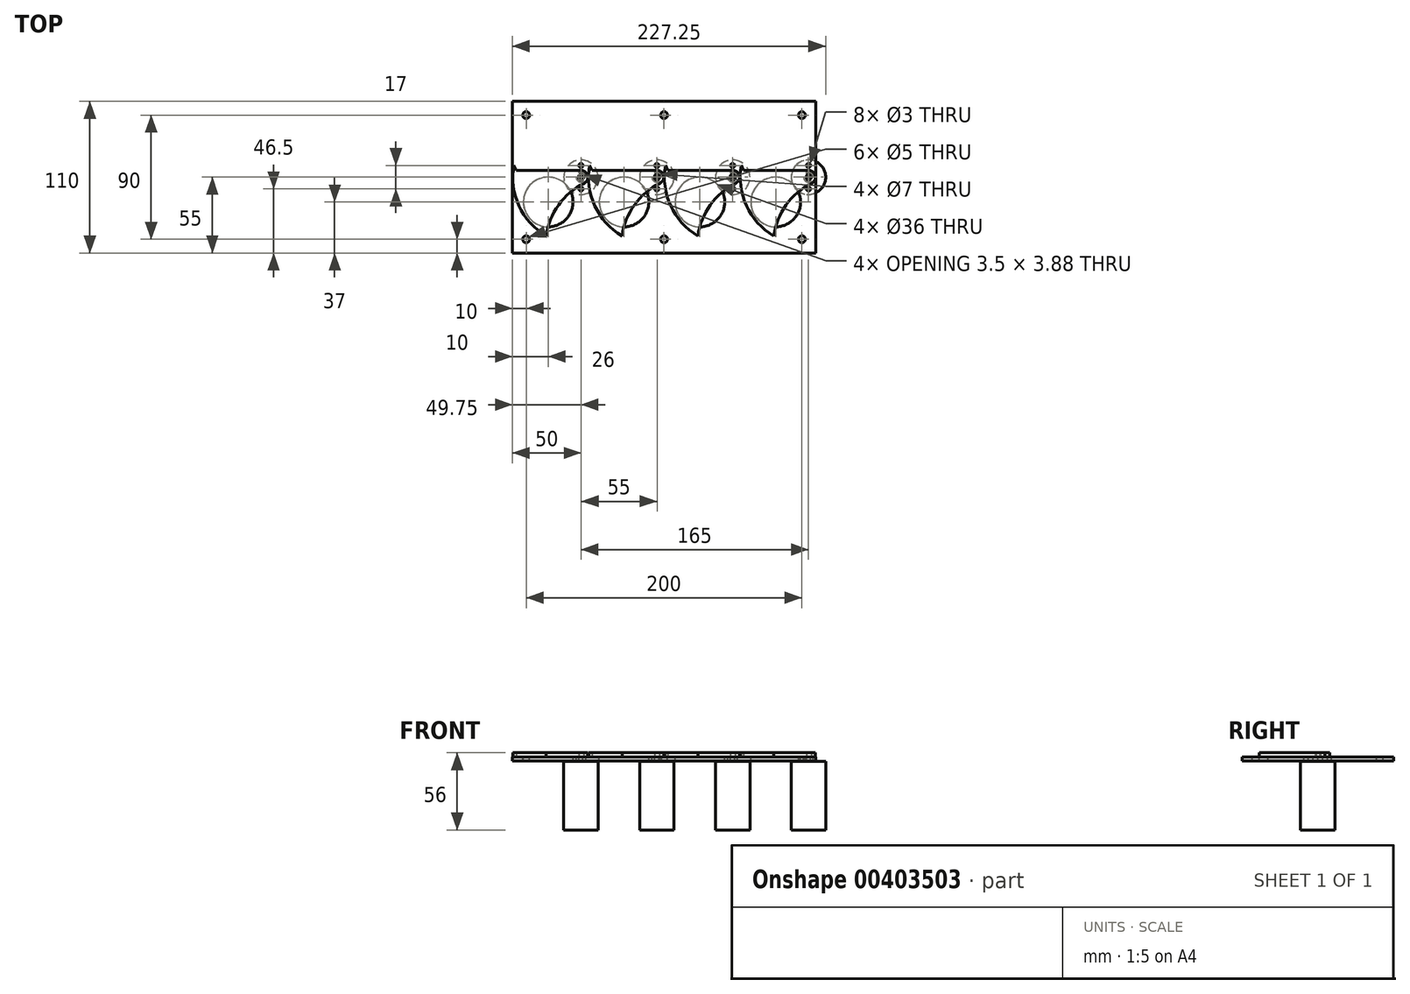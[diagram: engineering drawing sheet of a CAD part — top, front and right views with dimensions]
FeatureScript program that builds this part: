
annotation { "Feature Type Name" : "Feature", "Feature Type Description" : "" }
export const myFeature = defineFeature(function(context is Context, id is Id, definition is map)
    precondition{}
    {
        {
            var Q0;
            Q0=qCreatedBy(makeId("Top.planeOp"),FACE);
            var sketch = newSketch(context, id + "F0", { "sketchPlane" : qUnion([Q0])});
            skPoint(sketch, "E0.middle", {"position": v(0, 0) * mm});
            skLineSegment(sketch, "E1", {"start": v(-48.75, 8.6) * mm, "end": v(-47, 5) * mm});
            skLineSegment(sketch, "E2", {"start": v(-47, 5) * mm, "end": v(0, 5) * mm});
            skArc(sketch, "E3", {"start": v(0, 5) * mm, "mid": v(4.87, 1.14) * mm, "end": v(2.22, -4.48) * mm});
            skArc(sketch, "E4", {"start": v(-48.75, 8.6) * mm, "mid": v(-44.96, -20.7) * mm, "end": v(-25.16, -42.63) * mm});
            skLineSegment(sketch, "E5", {"start": v(-1.5, 1.32) * mm, "end": v(-1.5, -1.32) * mm});
            skArc(sketch, "E6", {"start": v(-1.5, -1.32) * mm, "mid": v(2, 0) * mm, "end": v(-1.5, 1.32) * mm});
            skArc(sketch, "E7", {"start": v(2.22, -4.48) * mm, "mid": v(-16.23, -20.14) * mm, "end": v(-25.16, -42.63) * mm});
            skArc(sketch, "E8.1.0.0", {"start": v(57.22, -4.48) * mm, "mid": v(38.77, -20.14) * mm, "end": v(29.84, -42.63) * mm});
            skArc(sketch, "E8.1.0.1", {"start": v(6.25, 8.6) * mm, "mid": v(10.04, -20.7) * mm, "end": v(29.84, -42.63) * mm});
            skLineSegment(sketch, "E8.1.0.2", {"start": v(8, 5) * mm, "end": v(55, 5) * mm});
            skPoint(sketch, "E8.1.0.3", {"position": v(55, 0) * mm});
            skArc(sketch, "E8.1.0.4", {"start": v(55, 5) * mm, "mid": v(59.87, 1.14) * mm, "end": v(57.22, -4.48) * mm});
            skLineSegment(sketch, "E8.1.0.5", {"start": v(6.25, 8.6) * mm, "end": v(8, 5) * mm});
            skLineSegment(sketch, "E8.1.0.6", {"start": v(53.5, 1.32) * mm, "end": v(53.5, -1.32) * mm});
            skArc(sketch, "E8.1.0.7", {"start": v(53.5, -1.32) * mm, "mid": v(57, 0) * mm, "end": v(53.5, 1.32) * mm});
            skArc(sketch, "E8.2.0.0", {"start": v(112.22, -4.48) * mm, "mid": v(93.77, -20.14) * mm, "end": v(84.84, -42.63) * mm});
            skArc(sketch, "E8.2.0.1", {"start": v(61.25, 8.6) * mm, "mid": v(65.04, -20.7) * mm, "end": v(84.84, -42.63) * mm});
            skLineSegment(sketch, "E8.2.0.2", {"start": v(63, 5) * mm, "end": v(110, 5) * mm});
            skPoint(sketch, "E8.2.0.3", {"position": v(110, 0) * mm});
            skArc(sketch, "E8.2.0.4", {"start": v(110, 5) * mm, "mid": v(114.87, 1.14) * mm, "end": v(112.22, -4.48) * mm});
            skLineSegment(sketch, "E8.2.0.5", {"start": v(61.25, 8.6) * mm, "end": v(63, 5) * mm});
            skLineSegment(sketch, "E8.2.0.6", {"start": v(108.5, 1.32) * mm, "end": v(108.5, -1.32) * mm});
            skArc(sketch, "E8.2.0.7", {"start": v(108.5, -1.32) * mm, "mid": v(112, 0) * mm, "end": v(108.5, 1.32) * mm});
            skArc(sketch, "E8.3.0.0", {"start": v(167.22, -4.48) * mm, "mid": v(148.77, -20.14) * mm, "end": v(139.84, -42.63) * mm});
            skArc(sketch, "E8.3.0.1", {"start": v(116.25, 8.6) * mm, "mid": v(120.04, -20.7) * mm, "end": v(139.84, -42.63) * mm});
            skLineSegment(sketch, "E8.3.0.2", {"start": v(118, 5) * mm, "end": v(165, 5) * mm});
            skPoint(sketch, "E8.3.0.3", {"position": v(165, 0) * mm});
            skArc(sketch, "E8.3.0.4", {"start": v(165, 5) * mm, "mid": v(169.87, 1.14) * mm, "end": v(167.22, -4.48) * mm});
            skLineSegment(sketch, "E8.3.0.5", {"start": v(116.25, 8.6) * mm, "end": v(118, 5) * mm});
            skLineSegment(sketch, "E8.3.0.6", {"start": v(163.5, 1.32) * mm, "end": v(163.5, -1.32) * mm});
            skArc(sketch, "E8.3.0.7", {"start": v(163.5, -1.32) * mm, "mid": v(167, 0) * mm, "end": v(163.5, 1.32) * mm});
            skLineSegment(sketch, "E8.direction1", {"start": v(-25.16, -42.63) * mm, "end": v(29.84, -42.63) * mm, "construction": true});
            skSolve(sketch);
        }
        {
            var Q0;
            Q0=qCreatedBy(makeId("Top.planeOp"),FACE);
            var sketch = newSketch(context, id + "F1", { "sketchPlane" : qUnion([Q0])});
            skCircle(sketch, "E9", {"center": v(0, 0) * mm, "radius": 3.5 * mm});
            skLineSegment(sketch, "E10.bottom", {"start": v(-49.75, 55) * mm, "end": v(170.25, 55) * mm});
            skLineSegment(sketch, "E10.top", {"start": v(-49.75, -55) * mm, "end": v(170.25, -55) * mm});
            skLineSegment(sketch, "E10.left", {"start": v(-49.75, 55) * mm, "end": v(-49.75, -55) * mm});
            skLineSegment(sketch, "E10.right", {"start": v(170.25, 55) * mm, "end": v(170.25, -55) * mm});
            skCircle(sketch, "E11", {"center": v(0, 8.5) * mm, "radius": 1.5 * mm});
            skCircle(sketch, "E12", {"center": v(0, -8.5) * mm, "radius": 1.5 * mm});
            skCircle(sketch, "E13", {"center": v(-39.75, -45) * mm, "radius": 2.5 * mm});
            skCircle(sketch, "E14", {"center": v(60.25, -45) * mm, "radius": 2.5 * mm});
            skCircle(sketch, "E15", {"center": v(160.25, -45) * mm, "radius": 2.5 * mm});
            skCircle(sketch, "E16", {"center": v(-39.75, 45) * mm, "radius": 2.5 * mm});
            skCircle(sketch, "E17", {"center": v(60.25, 45) * mm, "radius": 2.5 * mm});
            skCircle(sketch, "E18", {"center": v(160.25, 45) * mm, "radius": 2.5 * mm});
            skCircle(sketch, "E19", {"center": v(-23.75, -18) * mm, "radius": 18 * mm});
            skCircle(sketch, "E20.1.0.0", {"center": v(55, 0) * mm, "radius": 3.5 * mm});
            skCircle(sketch, "E20.1.0.1", {"center": v(31.25, -18) * mm, "radius": 18 * mm});
            skCircle(sketch, "E20.1.0.2", {"center": v(55, -8.5) * mm, "radius": 1.5 * mm});
            skCircle(sketch, "E20.1.0.3", {"center": v(55, 8.5) * mm, "radius": 1.5 * mm});
            skCircle(sketch, "E20.2.0.0", {"center": v(110, 0) * mm, "radius": 3.5 * mm});
            skCircle(sketch, "E20.2.0.1", {"center": v(86.25, -18) * mm, "radius": 18 * mm});
            skCircle(sketch, "E20.2.0.2", {"center": v(110, -8.5) * mm, "radius": 1.5 * mm});
            skCircle(sketch, "E20.2.0.3", {"center": v(110, 8.5) * mm, "radius": 1.5 * mm});
            skCircle(sketch, "E20.3.0.0", {"center": v(165, 0) * mm, "radius": 3.5 * mm});
            skCircle(sketch, "E20.3.0.1", {"center": v(141.25, -18) * mm, "radius": 18 * mm});
            skCircle(sketch, "E20.3.0.2", {"center": v(165, -8.5) * mm, "radius": 1.5 * mm});
            skCircle(sketch, "E20.3.0.3", {"center": v(165, 8.5) * mm, "radius": 1.5 * mm});
            skLineSegment(sketch, "E20.direction1", {"start": v(-23.75, -18) * mm, "end": v(31.25, -18) * mm, "construction": true});
            skSolve(sketch);
        }
        {
            var Q0;
            Q0=qCreatedBy(makeId("Top.planeOp"),FACE);
            var sketch = newSketch(context, id + "F2", { "sketchPlane" : qUnion([Q0])});
            skCircle(sketch, "E21", {"center": v(0, 0) * mm, "radius": 12.5 * mm});
            skCircle(sketch, "E22.1.0.0", {"center": v(55, 0) * mm, "radius": 12.5 * mm});
            skCircle(sketch, "E22.2.0.0", {"center": v(110, 0) * mm, "radius": 12.5 * mm});
            skCircle(sketch, "E22.3.0.0", {"center": v(165, 0) * mm, "radius": 12.5 * mm});
            skLineSegment(sketch, "E22.direction1", {"start": v(0, 0) * mm, "end": v(55, 0) * mm, "construction": true});
            skSolve(sketch);
        }
        {
            var Q0;
            Q0 = qSketchRegion(id + "F0", true);
            extrude(context, id + "F3", {"entities" : qUnion([Q0]), "depth" : 3 * mm});
        }
        {
            var Q0;
            Q0 = qSketchRegion(id + "F1", true);
            extrude(context, id + "F4", {"entities" : qUnion([Q0]), "oppositeDirection" : true, "depth" : 3 * mm});
        }
        {
            var Q0;
            Q0 = qSketchRegion(id + "F2", true);
            extrude(context, id + "F5", {"entities" : qUnion([Q0]), "oppositeDirection" : true, "depth" : 53 * mm, "hasSecondDirection" : true, "secondDirectionOppositeDirection" : true, "secondDirectionDepth" : 3.1 * mm});
        }
    });
